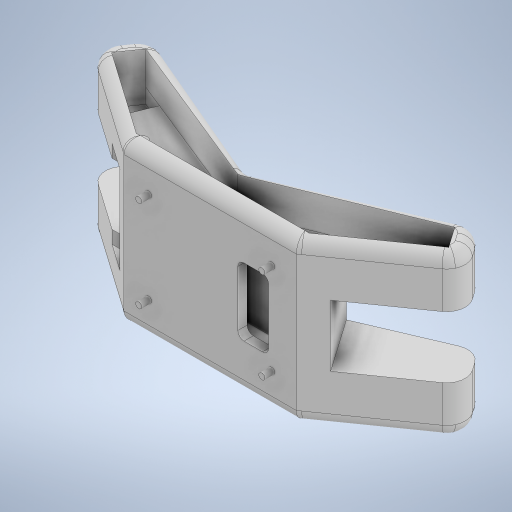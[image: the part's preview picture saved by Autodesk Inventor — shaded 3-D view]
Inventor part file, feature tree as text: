
AUTODESK INVENTOR PART (.ipt)
format: ipt  version: 2024 (Build 280153000, 153)  size: 569,856 bytes
history: native  units: mm
features: extrude x15, sketch x15, fillet x4, other x2
ambient origin geometry x8: Origin, YZ Plane, XZ Plane, XY Plane, X Axis, Y Axis, Z Axis, Center Point
bodies: Body1 (feature_tree)
feature tree (36):
  other  "Těleso1"
  extrude  "Vysunutí1"  Depth=140.0mm
  extrude  "Vysunutí2"  Depth=90.0mm
  extrude  "Vysunutí3"  Depth=30.0mm TaperAngle=0.0deg
  extrude  "Vysunutí7"  Depth=15.0mm
  extrude  "Vysunutí8"  Depth=71.0mm
  extrude  "Vysunutí9"  Depth=132.0mm TaperAngle=0.0deg
  other  "Pracovní rovina1"
  extrude  "Vysunutí10"  Depth=100.0mm
  extrude  "Vysunutí11"  Depth=74.0mm
  extrude  "Vysunutí12"  Depth=5.0mm
  extrude  "Vysunutí13"  Depth=20.0mm
  fillet  "Zaoblení1"  Radius=8.0mm
  fillet  "Zaoblení2"  Radius=100.0mm
  extrude  "Vysunutí14"  Depth=6.108652mm
  extrude  "Vysunutí16"  Depth=35.0mm
  fillet  "Zaoblení3"  Radius=100.0mm
  fillet  "Zaoblení4"  Radius=25.307274mm
  extrude  "Vysunutí17"  Depth=35.0mm
  extrude  "Vysunutí18"  Depth=20.0mm TaperAngle=0.0deg
  extrude  "Vysunutí19"  Depth=160.0mm
  sketch  "Náčrt1"
  sketch  "Náčrt2"
  sketch  "Náčrt3"
  sketch  "Náčrt7"
  sketch  "Náčrt8"
  sketch  "Náčrt9"
  sketch  "Náčrt11"
  sketch  "Náčrt12"
  sketch  "Náčrt13"
  sketch  "Náčrt14"
  sketch  "Náčrt17"
  sketch  "Náčrt19"
  sketch  "Náčrt20"
  sketch  "Náčrt21"
  sketch  "Náčrt23"
